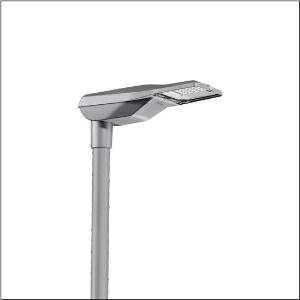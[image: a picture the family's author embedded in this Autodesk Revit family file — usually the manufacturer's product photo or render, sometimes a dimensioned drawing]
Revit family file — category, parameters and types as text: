
# Revit family: streetlight_sl_21_iq_micro___stw1_0a_5xe1e31d08db_99ec
name_source: partatom
category: Lighting Fixtures
units: mm (PartAtom-declared; Revit-internal decimal feet)

## family parameters
Cut with Voids When Loaded = No
Host = Face
Light Source = No
Part Type = Normal
Room Calculation Point = No
Round Connector Dimension = Use Diameter
Shared = No

## types (1)
- --- (1 x LED, 4810 lm, 36.4 W, 3000K)
    Apparent Load = 36 VA
    CIE Flux Codes = 38 75 98 100 100
    Color Rendering = 70
    Color Temperature = 3000K
    Default Elevation = 1800 mm
    Description = Streetlight SL 21 iQ micro, mast luminaire, primary light control with lens, of PMMA, primary optical cover: cover, of toughened safety glass, transparent, light distribution: STW1.0a, light emission: direct distribution, primary light characteristic: asymmetric, installation type: post-top, side-entry, LED, High Power LED, rated luminous flux: 4.810lm, luminous efficacy: 132lm/W, light colour: 730, colour temperature: 3000K, control: Auto-Match, Temp-Guard, Lumen-Switch, Night-Set, Smart-Wire, Light-Fading, Desk-Remote (wireless, voltage-free reading and setting of iQ features in the workshop via application-optimized NFC function/RFID function), optimised constant luminous flux control (CLO 2.0), presetting dimming linear, mains connection: 220..240V, AC, 50/60Hz, start of lifetime: 36W, end of service life: 38W, reduction: 16W, luminaire housing, of diecast aluminium, powder-coated, Siteco® metallic grey (DB 702S), corrosivity category C5 mid according to DIN EN ISO 12944, please order mast flange separately, inclination adjustable: 0°, 5°, 10°, 15°, sealing non-destructively replaceable, multi-level sealing system, length: 528mm, width: 235mm, height: 110mm, mast flange for spigot size: 42mm (side-entry): 5XC10008XM4, 60/48mm (side-entry/post-top): 5XC10108XM2, 76/60mm (side-entry/post-top): 5XC10108XM1, protection rating (complete): IP66, insulation class (complete): insulation class II (safety insulation), certification: CE, ENEC, ENEC+, VDE, impact resistance: IK09, permissible operating ambient temperature for outdoor applications: -40..+50°C, standard-compliant lighting for roads and squares, packaging unit: 1 piece

Light Distribution: STW1.0a
    Height = 110 mm
    Lamp = 1 x LED
    Lamp Light Flux = 4810 lm
    Lamp Power = 36.4 W
    Lamp count = 1
    Length = 528 mm
    Luminous efficacy = 132 lm/W
    Manufacturer = Siteco
    ModVariant = No
    Model = 5XE1E31D08DB
    Number of Poles = 1
    OnlyDefault = Yes
    Power Factor = 1
    Product Name = Streetlight SL 21 iQ micro | STW1.0a
    Product group = mast luminaire | pylon top
    ProductGroupID = 6100
    Protection Class = Protection class II
    Protection Degree = IP 66
    RLX_Detail_Level = 1
    RLX_Emergency_Light_Flux = 0 lm
    RLX_Emergency_Type = 0
    RLX_Emergency_Type_DB = No
    RlxData = <blob elided: 99421 chars, md5=a434ccb6>
    Socket = socket
    Standby Power = 0 W
    System Light Flux = 4810 lm
    System Power = 36 W
    Type Comments = factory setting: luminous flux: 100 % | dim-lin: 254 | 715 mA
    Type Image = l_1006881.jpg
    URL = http://relux.com
    VarID = @adj_105655
    Voltage = 0 V
    Weight = 0.00 kg
    Width = 235 mm

## geometry (parser evidence)
native form markers: Blend x4, Sweep x11
no freeform markers — native parametric forms only
